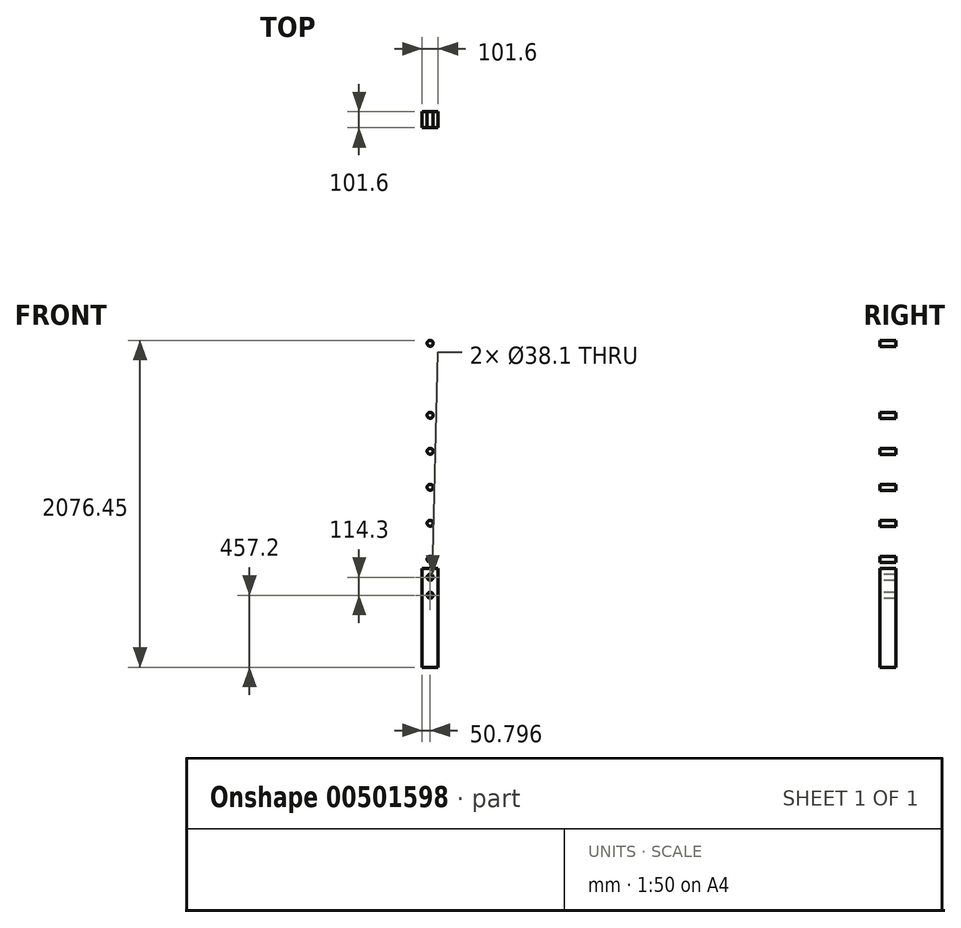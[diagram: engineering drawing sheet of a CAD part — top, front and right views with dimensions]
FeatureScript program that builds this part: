
annotation { "Feature Type Name" : "Feature", "Feature Type Description" : "" }
export const myFeature = defineFeature(function(context is Context, id is Id, definition is map)
    precondition{}
    {
        {
            var Q0;
            Q0=qCreatedBy(makeId("Front.planeOp"),FACE);
            var sketch = newSketch(context, id + "F0", { "sketchPlane" : qUnion([Q0])});
            skLineSegment(sketch, "E0.bottom", {"start": v(-26.27, -188.77) * mm, "end": v(75.33, -188.77) * mm});
            skLineSegment(sketch, "E0.top", {"start": v(-26.27, 2249.63) * mm, "end": v(75.33, 2249.63) * mm});
            skLineSegment(sketch, "E0.left", {"start": v(-26.27, -188.77) * mm, "end": v(-26.27, 2249.63) * mm});
            skLineSegment(sketch, "E0.right", {"start": v(75.33, -188.77) * mm, "end": v(75.33, 2249.63) * mm});
            skSolve(sketch);
        }
        {
            var Q0;
            Q0=makeQuery(id+"F0.imprint","IMPRINT",FACE,{"disambiguationData":[TD([[makeQuery(id+"F0.imprint","IMPRINT",EDGE,{"derivedFrom":sQuery(id+"F0.wireOp",EDGE,"E0.bottom")}),1.0]])]});
            extrude(context, id + "F1", {"entities" : qUnion([Q0]), "depth" : 101.6 * mm, "offsetDistance" : 25.4 * mm});
        }
        {
            var Q0;
            Q0=makeQuery(id+"F1.opExtrude","CAP_FACE",FACE,{"disambiguationData":[OSD([sQuery(id+"F0.wireOp",EDGE,"E0.bottom"),sQuery(id+"F0.wireOp",EDGE,"E0.top"),sQuery(id+"F0.wireOp",EDGE,"E0.left"),sQuery(id+"F0.wireOp",EDGE,"E0.right")])],"isStart":false});
            var sketch = newSketch(context, id + "F2", { "sketchPlane" : qUnion([Q0])});
            skLineSegment(sketch, "E1", {"start": v(24.53, -188.77) * mm, "end": v(24.53, 268.43) * mm});
            skCircle(sketch, "E2", {"center": v(24.53, 268.43) * mm, "radius": 19.05 * mm});
            skLineSegment(sketch, "E3", {"start": v(24.53, 268.43) * mm, "end": v(24.53, 2249.63) * mm});
            skCircle(sketch, "E4", {"center": v(24.53, 382.73) * mm, "radius": 19.05 * mm});
            skLineSegment(sketch, "E5", {"start": v(-26.27, 439.88) * mm, "end": v(75.33, 439.88) * mm});
            skCircle(sketch, "E6.MirrorC", {"center": v(24.53, 497.03) * mm, "radius": 19.05 * mm});
            skCircle(sketch, "E7.MirrorC", {"center": v(24.53, 611.33) * mm, "radius": 19.05 * mm});
            skLineSegment(sketch, "E8", {"start": v(-26.27, 668.48) * mm, "end": v(75.33, 668.48) * mm});
            skCircle(sketch, "E9.MirrorC", {"center": v(24.53, 725.63) * mm, "radius": 19.05 * mm});
            skCircle(sketch, "E10.MirrorC", {"center": v(24.53, 839.93) * mm, "radius": 19.05 * mm});
            skCircle(sketch, "E11.MirrorC", {"center": v(24.53, 954.23) * mm, "radius": 19.05 * mm});
            skCircle(sketch, "E12.MirrorC", {"center": v(24.53, 1068.53) * mm, "radius": 19.05 * mm});
            skLineSegment(sketch, "E13", {"start": v(-26.27, 1125.68) * mm, "end": v(75.33, 1125.68) * mm});
            skCircle(sketch, "E14.MirrorC", {"center": v(24.53, 1182.83) * mm, "radius": 19.05 * mm});
            skCircle(sketch, "E15.MirrorC", {"center": v(24.53, 1297.13) * mm, "radius": 19.05 * mm});
            skCircle(sketch, "E16.MirrorC", {"center": v(24.53, 1411.43) * mm, "radius": 19.05 * mm});
            skCircle(sketch, "E17.MirrorC", {"center": v(24.53, 1525.73) * mm, "radius": 19.05 * mm});
            skCircle(sketch, "E18.MirrorC", {"center": v(24.53, 1640.03) * mm, "radius": 19.05 * mm});
            skCircle(sketch, "E19.MirrorC", {"center": v(24.53, 1754.33) * mm, "radius": 19.05 * mm});
            skCircle(sketch, "E20.MirrorC", {"center": v(24.53, 1868.63) * mm, "radius": 19.05 * mm});
            skSolve(sketch);
        }
        {
            var Q0;
            {var subQ0=sQuery(id+"F2.wireOp",EDGE,"E20.MirrorC");var subQ1=sQuery(id+"F2.wireOp",EDGE,"E3");var subQ2=makeQuery(id+"F2.imprint","INTERSECT",VERTEX,{"disambiguationData":[OD(0.0)],"derivedFrom":[subQ1,subQ0]});Q0=makeQuery(id+"F2.imprint","IMPRINT",FACE,{"disambiguationData":[TD([[makeQuery(id+"F2.imprint","IMPRINT",EDGE,{"disambiguationData":[TD([[subQ2,-1.0]])],"derivedFrom":subQ1}),1.0]])]});}
            var Q1;
            {var subQ0=sQuery(id+"F2.wireOp",EDGE,"E20.MirrorC");var subQ1=sQuery(id+"F2.wireOp",EDGE,"E3");var subQ2=makeQuery(id+"F2.imprint","INTERSECT",VERTEX,{"disambiguationData":[OD(0.0)],"derivedFrom":[subQ1,subQ0]});Q1=makeQuery(id+"F2.imprint","IMPRINT",FACE,{"disambiguationData":[TD([[makeQuery(id+"F2.imprint","IMPRINT",EDGE,{"disambiguationData":[TD([[subQ2,-1.0]])],"derivedFrom":subQ1}),-1.0]])]});}
            var Q2;
            {var subQ0=sQuery(id+"F2.wireOp",EDGE,"E19.MirrorC");var subQ1=sQuery(id+"F2.wireOp",EDGE,"E3");var subQ2=makeQuery(id+"F2.imprint","INTERSECT",VERTEX,{"disambiguationData":[OD(0.0)],"derivedFrom":[subQ1,subQ0]});Q2=makeQuery(id+"F2.imprint","IMPRINT",FACE,{"disambiguationData":[TD([[makeQuery(id+"F2.imprint","IMPRINT",EDGE,{"disambiguationData":[TD([[subQ2,-1.0]])],"derivedFrom":subQ1}),1.0]])]});}
            var Q3;
            {var subQ0=sQuery(id+"F2.wireOp",EDGE,"E19.MirrorC");var subQ1=sQuery(id+"F2.wireOp",EDGE,"E3");var subQ2=makeQuery(id+"F2.imprint","INTERSECT",VERTEX,{"disambiguationData":[OD(0.0)],"derivedFrom":[subQ1,subQ0]});Q3=makeQuery(id+"F2.imprint","IMPRINT",FACE,{"disambiguationData":[TD([[makeQuery(id+"F2.imprint","IMPRINT",EDGE,{"disambiguationData":[TD([[subQ2,-1.0]])],"derivedFrom":subQ1}),-1.0]])]});}
            var Q4;
            {var subQ0=sQuery(id+"F2.wireOp",EDGE,"E18.MirrorC");var subQ1=sQuery(id+"F2.wireOp",EDGE,"E3");var subQ2=makeQuery(id+"F2.imprint","INTERSECT",VERTEX,{"disambiguationData":[OD(0.0)],"derivedFrom":[subQ1,subQ0]});Q4=makeQuery(id+"F2.imprint","IMPRINT",FACE,{"disambiguationData":[TD([[makeQuery(id+"F2.imprint","IMPRINT",EDGE,{"disambiguationData":[TD([[subQ2,-1.0]])],"derivedFrom":subQ1}),1.0]])]});}
            var Q5;
            {var subQ0=sQuery(id+"F2.wireOp",EDGE,"E18.MirrorC");var subQ1=sQuery(id+"F2.wireOp",EDGE,"E3");var subQ2=makeQuery(id+"F2.imprint","INTERSECT",VERTEX,{"disambiguationData":[OD(0.0)],"derivedFrom":[subQ1,subQ0]});Q5=makeQuery(id+"F2.imprint","IMPRINT",FACE,{"disambiguationData":[TD([[makeQuery(id+"F2.imprint","IMPRINT",EDGE,{"disambiguationData":[TD([[subQ2,-1.0]])],"derivedFrom":subQ1}),-1.0]])]});}
            var Q6;
            {var subQ0=sQuery(id+"F2.wireOp",EDGE,"E17.MirrorC");var subQ1=sQuery(id+"F2.wireOp",EDGE,"E3");var subQ2=makeQuery(id+"F2.imprint","INTERSECT",VERTEX,{"disambiguationData":[OD(0.0)],"derivedFrom":[subQ1,subQ0]});Q6=makeQuery(id+"F2.imprint","IMPRINT",FACE,{"disambiguationData":[TD([[makeQuery(id+"F2.imprint","IMPRINT",EDGE,{"disambiguationData":[TD([[subQ2,-1.0]])],"derivedFrom":subQ1}),1.0]])]});}
            var Q7;
            {var subQ0=sQuery(id+"F2.wireOp",EDGE,"E16.MirrorC");var subQ1=sQuery(id+"F2.wireOp",EDGE,"E3");var subQ2=makeQuery(id+"F2.imprint","INTERSECT",VERTEX,{"disambiguationData":[OD(0.0)],"derivedFrom":[subQ1,subQ0]});Q7=makeQuery(id+"F2.imprint","IMPRINT",FACE,{"disambiguationData":[TD([[makeQuery(id+"F2.imprint","IMPRINT",EDGE,{"disambiguationData":[TD([[subQ2,-1.0]])],"derivedFrom":subQ1}),-1.0]])]});}
            var Q8;
            {var subQ0=sQuery(id+"F2.wireOp",EDGE,"E16.MirrorC");var subQ1=sQuery(id+"F2.wireOp",EDGE,"E3");var subQ2=makeQuery(id+"F2.imprint","INTERSECT",VERTEX,{"disambiguationData":[OD(0.0)],"derivedFrom":[subQ1,subQ0]});Q8=makeQuery(id+"F2.imprint","IMPRINT",FACE,{"disambiguationData":[TD([[makeQuery(id+"F2.imprint","IMPRINT",EDGE,{"disambiguationData":[TD([[subQ2,-1.0]])],"derivedFrom":subQ1}),1.0]])]});}
            var Q9;
            {var subQ0=sQuery(id+"F2.wireOp",EDGE,"E17.MirrorC");var subQ1=sQuery(id+"F2.wireOp",EDGE,"E3");var subQ2=makeQuery(id+"F2.imprint","INTERSECT",VERTEX,{"disambiguationData":[OD(0.0)],"derivedFrom":[subQ1,subQ0]});Q9=makeQuery(id+"F2.imprint","IMPRINT",FACE,{"disambiguationData":[TD([[makeQuery(id+"F2.imprint","IMPRINT",EDGE,{"disambiguationData":[TD([[subQ2,-1.0]])],"derivedFrom":subQ1}),-1.0]])]});}
            var Q10;
            {var subQ0=sQuery(id+"F2.wireOp",EDGE,"E15.MirrorC");var subQ1=sQuery(id+"F2.wireOp",EDGE,"E3");var subQ2=makeQuery(id+"F2.imprint","INTERSECT",VERTEX,{"disambiguationData":[OD(0.0)],"derivedFrom":[subQ1,subQ0]});Q10=makeQuery(id+"F2.imprint","IMPRINT",FACE,{"disambiguationData":[TD([[makeQuery(id+"F2.imprint","IMPRINT",EDGE,{"disambiguationData":[TD([[subQ2,-1.0]])],"derivedFrom":subQ1}),-1.0]])]});}
            var Q11;
            {var subQ0=sQuery(id+"F2.wireOp",EDGE,"E15.MirrorC");var subQ1=sQuery(id+"F2.wireOp",EDGE,"E3");var subQ2=makeQuery(id+"F2.imprint","INTERSECT",VERTEX,{"disambiguationData":[OD(0.0)],"derivedFrom":[subQ1,subQ0]});Q11=makeQuery(id+"F2.imprint","IMPRINT",FACE,{"disambiguationData":[TD([[makeQuery(id+"F2.imprint","IMPRINT",EDGE,{"disambiguationData":[TD([[subQ2,-1.0]])],"derivedFrom":subQ1}),1.0]])]});}
            var Q12;
            {var subQ0=sQuery(id+"F2.wireOp",EDGE,"E14.MirrorC");var subQ1=sQuery(id+"F2.wireOp",EDGE,"E3");var subQ2=makeQuery(id+"F2.imprint","INTERSECT",VERTEX,{"disambiguationData":[OD(0.0)],"derivedFrom":[subQ1,subQ0]});Q12=makeQuery(id+"F2.imprint","IMPRINT",FACE,{"disambiguationData":[TD([[makeQuery(id+"F2.imprint","IMPRINT",EDGE,{"disambiguationData":[TD([[subQ2,-1.0]])],"derivedFrom":subQ1}),1.0]])]});}
            var Q13;
            {var subQ0=sQuery(id+"F2.wireOp",EDGE,"E14.MirrorC");var subQ1=sQuery(id+"F2.wireOp",EDGE,"E3");var subQ2=makeQuery(id+"F2.imprint","INTERSECT",VERTEX,{"disambiguationData":[OD(0.0)],"derivedFrom":[subQ1,subQ0]});Q13=makeQuery(id+"F2.imprint","IMPRINT",FACE,{"disambiguationData":[TD([[makeQuery(id+"F2.imprint","IMPRINT",EDGE,{"disambiguationData":[TD([[subQ2,-1.0]])],"derivedFrom":subQ1}),-1.0]])]});}
            var Q14;
            {var subQ0=sQuery(id+"F2.wireOp",EDGE,"E12.MirrorC");var subQ1=sQuery(id+"F2.wireOp",EDGE,"E3");var subQ2=makeQuery(id+"F2.imprint","INTERSECT",VERTEX,{"disambiguationData":[OD(0.0)],"derivedFrom":[subQ1,subQ0]});Q14=makeQuery(id+"F2.imprint","IMPRINT",FACE,{"disambiguationData":[TD([[makeQuery(id+"F2.imprint","IMPRINT",EDGE,{"disambiguationData":[TD([[subQ2,-1.0]])],"derivedFrom":subQ1}),-1.0]])]});}
            var Q15;
            {var subQ0=sQuery(id+"F2.wireOp",EDGE,"E12.MirrorC");var subQ1=sQuery(id+"F2.wireOp",EDGE,"E3");var subQ2=makeQuery(id+"F2.imprint","INTERSECT",VERTEX,{"disambiguationData":[OD(0.0)],"derivedFrom":[subQ1,subQ0]});Q15=makeQuery(id+"F2.imprint","IMPRINT",FACE,{"disambiguationData":[TD([[makeQuery(id+"F2.imprint","IMPRINT",EDGE,{"disambiguationData":[TD([[subQ2,-1.0]])],"derivedFrom":subQ1}),1.0]])]});}
            var Q16;
            {var subQ0=sQuery(id+"F2.wireOp",EDGE,"E11.MirrorC");var subQ1=sQuery(id+"F2.wireOp",EDGE,"E3");var subQ2=makeQuery(id+"F2.imprint","INTERSECT",VERTEX,{"disambiguationData":[OD(0.0)],"derivedFrom":[subQ1,subQ0]});Q16=makeQuery(id+"F2.imprint","IMPRINT",FACE,{"disambiguationData":[TD([[makeQuery(id+"F2.imprint","IMPRINT",EDGE,{"disambiguationData":[TD([[subQ2,-1.0]])],"derivedFrom":subQ1}),1.0]])]});}
            var Q17;
            {var subQ0=sQuery(id+"F2.wireOp",EDGE,"E11.MirrorC");var subQ1=sQuery(id+"F2.wireOp",EDGE,"E3");var subQ2=makeQuery(id+"F2.imprint","INTERSECT",VERTEX,{"disambiguationData":[OD(0.0)],"derivedFrom":[subQ1,subQ0]});Q17=makeQuery(id+"F2.imprint","IMPRINT",FACE,{"disambiguationData":[TD([[makeQuery(id+"F2.imprint","IMPRINT",EDGE,{"disambiguationData":[TD([[subQ2,-1.0]])],"derivedFrom":subQ1}),-1.0]])]});}
            var Q18;
            {var subQ0=sQuery(id+"F2.wireOp",EDGE,"E10.MirrorC");var subQ1=sQuery(id+"F2.wireOp",EDGE,"E3");var subQ2=makeQuery(id+"F2.imprint","INTERSECT",VERTEX,{"disambiguationData":[OD(0.0)],"derivedFrom":[subQ1,subQ0]});Q18=makeQuery(id+"F2.imprint","IMPRINT",FACE,{"disambiguationData":[TD([[makeQuery(id+"F2.imprint","IMPRINT",EDGE,{"disambiguationData":[TD([[subQ2,-1.0]])],"derivedFrom":subQ1}),1.0]])]});}
            var Q19;
            {var subQ0=sQuery(id+"F2.wireOp",EDGE,"E10.MirrorC");var subQ1=sQuery(id+"F2.wireOp",EDGE,"E3");var subQ2=makeQuery(id+"F2.imprint","INTERSECT",VERTEX,{"disambiguationData":[OD(0.0)],"derivedFrom":[subQ1,subQ0]});Q19=makeQuery(id+"F2.imprint","IMPRINT",FACE,{"disambiguationData":[TD([[makeQuery(id+"F2.imprint","IMPRINT",EDGE,{"disambiguationData":[TD([[subQ2,-1.0]])],"derivedFrom":subQ1}),-1.0]])]});}
            var Q20;
            {var subQ0=sQuery(id+"F2.wireOp",EDGE,"E9.MirrorC");var subQ1=sQuery(id+"F2.wireOp",EDGE,"E3");var subQ2=makeQuery(id+"F2.imprint","INTERSECT",VERTEX,{"disambiguationData":[OD(0.0)],"derivedFrom":[subQ1,subQ0]});Q20=makeQuery(id+"F2.imprint","IMPRINT",FACE,{"disambiguationData":[TD([[makeQuery(id+"F2.imprint","IMPRINT",EDGE,{"disambiguationData":[TD([[subQ2,-1.0]])],"derivedFrom":subQ1}),1.0]])]});}
            var Q21;
            {var subQ0=sQuery(id+"F2.wireOp",EDGE,"E9.MirrorC");var subQ1=sQuery(id+"F2.wireOp",EDGE,"E3");var subQ2=makeQuery(id+"F2.imprint","INTERSECT",VERTEX,{"disambiguationData":[OD(0.0)],"derivedFrom":[subQ1,subQ0]});Q21=makeQuery(id+"F2.imprint","IMPRINT",FACE,{"disambiguationData":[TD([[makeQuery(id+"F2.imprint","IMPRINT",EDGE,{"disambiguationData":[TD([[subQ2,-1.0]])],"derivedFrom":subQ1}),-1.0]])]});}
            var Q22;
            {var subQ0=sQuery(id+"F2.wireOp",EDGE,"E7.MirrorC");var subQ1=sQuery(id+"F2.wireOp",EDGE,"E3");var subQ2=makeQuery(id+"F2.imprint","INTERSECT",VERTEX,{"disambiguationData":[OD(0.0)],"derivedFrom":[subQ1,subQ0]});Q22=makeQuery(id+"F2.imprint","IMPRINT",FACE,{"disambiguationData":[TD([[makeQuery(id+"F2.imprint","IMPRINT",EDGE,{"disambiguationData":[TD([[subQ2,-1.0]])],"derivedFrom":subQ1}),1.0]])]});}
            var Q23;
            {var subQ0=sQuery(id+"F2.wireOp",EDGE,"E7.MirrorC");var subQ1=sQuery(id+"F2.wireOp",EDGE,"E3");var subQ2=makeQuery(id+"F2.imprint","INTERSECT",VERTEX,{"disambiguationData":[OD(0.0)],"derivedFrom":[subQ1,subQ0]});Q23=makeQuery(id+"F2.imprint","IMPRINT",FACE,{"disambiguationData":[TD([[makeQuery(id+"F2.imprint","IMPRINT",EDGE,{"disambiguationData":[TD([[subQ2,-1.0]])],"derivedFrom":subQ1}),-1.0]])]});}
            var Q24;
            {var subQ0=sQuery(id+"F2.wireOp",EDGE,"E6.MirrorC");var subQ1=sQuery(id+"F2.wireOp",EDGE,"E3");var subQ2=makeQuery(id+"F2.imprint","INTERSECT",VERTEX,{"disambiguationData":[OD(0.0)],"derivedFrom":[subQ1,subQ0]});Q24=makeQuery(id+"F2.imprint","IMPRINT",FACE,{"disambiguationData":[TD([[makeQuery(id+"F2.imprint","IMPRINT",EDGE,{"disambiguationData":[TD([[subQ2,-1.0]])],"derivedFrom":subQ1}),1.0]])]});}
            var Q25;
            {var subQ0=sQuery(id+"F2.wireOp",EDGE,"E6.MirrorC");var subQ1=sQuery(id+"F2.wireOp",EDGE,"E3");var subQ2=makeQuery(id+"F2.imprint","INTERSECT",VERTEX,{"disambiguationData":[OD(0.0)],"derivedFrom":[subQ1,subQ0]});Q25=makeQuery(id+"F2.imprint","IMPRINT",FACE,{"disambiguationData":[TD([[makeQuery(id+"F2.imprint","IMPRINT",EDGE,{"disambiguationData":[TD([[subQ2,-1.0]])],"derivedFrom":subQ1}),-1.0]])]});}
            var Q26;
            {var subQ0=sQuery(id+"F2.wireOp",EDGE,"E4");var subQ1=sQuery(id+"F2.wireOp",EDGE,"E3");var subQ2=makeQuery(id+"F2.imprint","INTERSECT",VERTEX,{"disambiguationData":[OD(0.0)],"derivedFrom":[subQ1,subQ0]});Q26=makeQuery(id+"F2.imprint","IMPRINT",FACE,{"disambiguationData":[TD([[makeQuery(id+"F2.imprint","IMPRINT",EDGE,{"disambiguationData":[TD([[subQ2,-1.0]])],"derivedFrom":subQ1}),1.0]])]});}
            var Q27;
            {var subQ0=sQuery(id+"F2.wireOp",EDGE,"E4");var subQ1=sQuery(id+"F2.wireOp",EDGE,"E3");var subQ2=makeQuery(id+"F2.imprint","INTERSECT",VERTEX,{"disambiguationData":[OD(0.0)],"derivedFrom":[subQ1,subQ0]});Q27=makeQuery(id+"F2.imprint","IMPRINT",FACE,{"disambiguationData":[TD([[makeQuery(id+"F2.imprint","IMPRINT",EDGE,{"disambiguationData":[TD([[subQ2,-1.0]])],"derivedFrom":subQ1}),-1.0]])]});}
            var Q28;
            {var subQ0=sQuery(id+"F2.wireOp",EDGE,"E3");var subQ1=sQuery(id+"F2.wireOp",EDGE,"E1");var subQ2=makeQuery(id+"F2.imprint","INTERSECT",VERTEX,{"derivedFrom":[subQ1,subQ0]});Q28=makeQuery(id+"F2.imprint","IMPRINT",FACE,{"disambiguationData":[TD([[makeQuery(id+"F2.imprint","IMPRINT",EDGE,{"disambiguationData":[TD([[subQ2,1.0]])],"derivedFrom":subQ1}),1.0]])]});}
            var Q29;
            {var subQ0=sQuery(id+"F2.wireOp",EDGE,"E3");var subQ1=sQuery(id+"F2.wireOp",EDGE,"E1");var subQ2=makeQuery(id+"F2.imprint","INTERSECT",VERTEX,{"derivedFrom":[subQ1,subQ0]});Q29=makeQuery(id+"F2.imprint","IMPRINT",FACE,{"disambiguationData":[TD([[makeQuery(id+"F2.imprint","IMPRINT",EDGE,{"disambiguationData":[TD([[subQ2,1.0]])],"derivedFrom":subQ1}),-1.0]])]});}
            extrude(context, id + "F3", {"entities" : qUnion([Q0, Q1, Q2, Q3, Q4, Q5, Q6, Q7, Q8, Q9, Q10, Q11, Q12, Q13, Q14, Q15, Q16, Q17, Q18, Q19, Q20, Q21, Q22, Q23, Q24, Q25, Q26, Q27, Q28, Q29]), "operationType" : NewBodyOperationType.REMOVE, "oppositeDirection" : true, "depth" : 101.6 * mm, "offsetDistance" : 25.4 * mm});
        }
    });
